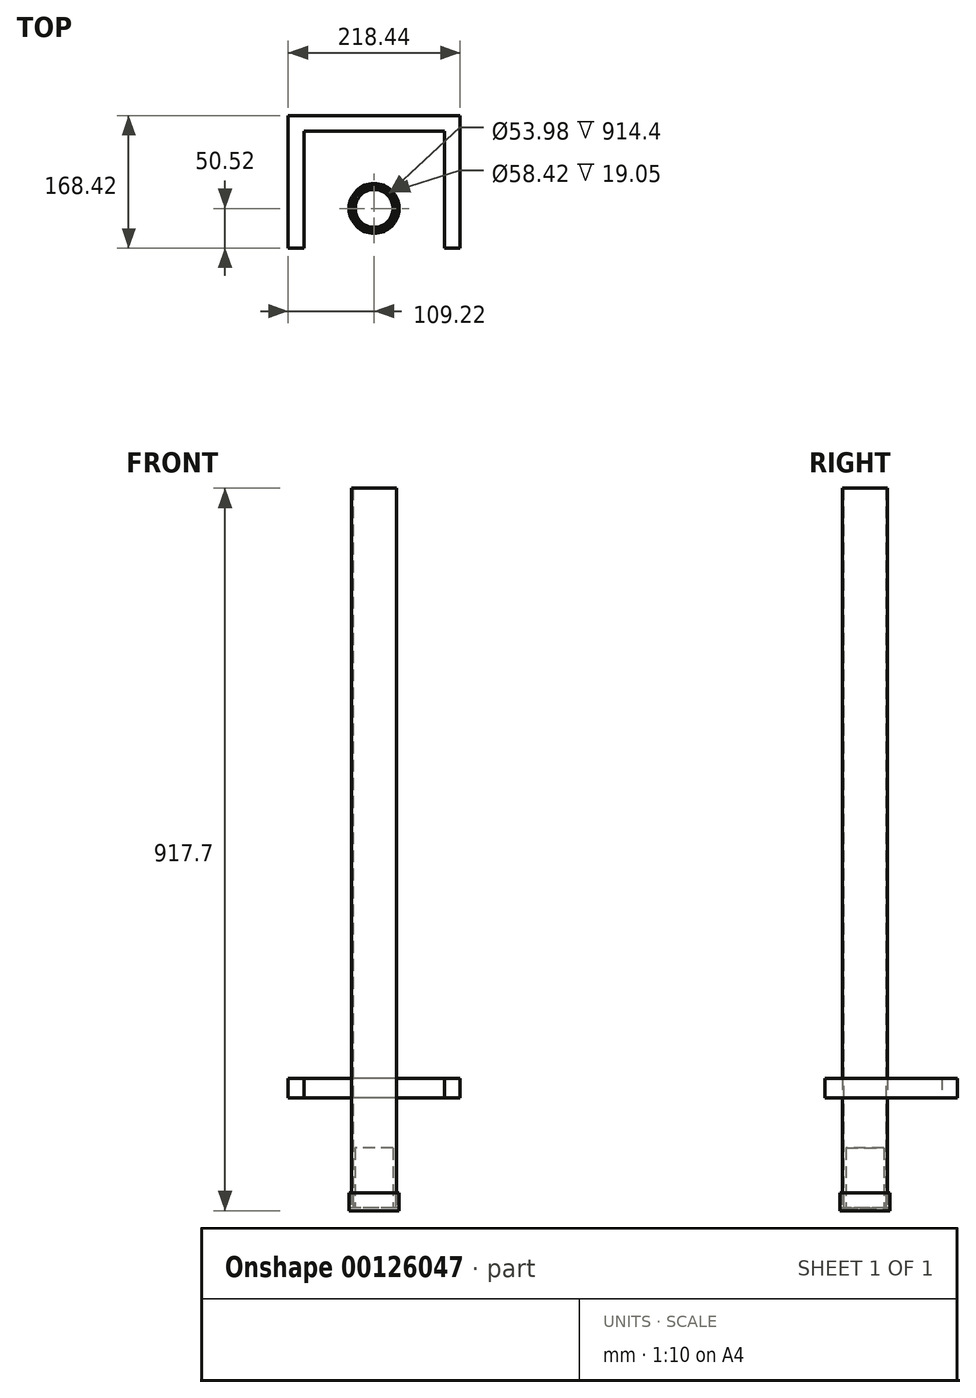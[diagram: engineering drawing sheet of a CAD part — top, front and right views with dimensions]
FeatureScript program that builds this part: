
annotation { "Feature Type Name" : "Feature", "Feature Type Description" : "" }
export const myFeature = defineFeature(function(context is Context, id is Id, definition is map)
    precondition{}
    {
        {
            var Q0;
            Q0=qCreatedBy(makeId("Top.planeOp"),FACE);
            var sketch = newSketch(context, id + "F0", { "sketchPlane" : qUnion([Q0])});
            skCircle(sketch, "E0", {"center": v(0, 0) * mm, "radius": 28.58 * mm});
            skCircle(sketch, "E1", {"center": v(0, 0) * mm, "radius": 26.99 * mm});
            skSolve(sketch);
        }
        {
            var Q0;
            Q0 = qSketchRegion(id + "F0", true);
            extrude(context, id + "F1", {"entities" : qUnion([Q0]), "depth" : 914.4 * mm});
        }
        {
            var Q0;
            Q0=qCreatedBy(makeId("Top.planeOp"),FACE);
            var sketch = newSketch(context, id + "F2", { "sketchPlane" : qUnion([Q0])});
            skCircle(sketch, "E2", {"center": v(0, 0) * mm, "radius": 24 * mm});
            skSolve(sketch);
        }
        {
            var Q0;
            Q0 = qSketchRegion(id + "F2", true);
            var Q1;
            Q1=makeQuery(id+"F2.imprint","IMPRINT",FACE,{"disambiguationData":[TD([[makeQuery(id+"F2.imprint","IMPRINT",EDGE,{"derivedFrom":sQuery(id+"F2.wireOp",EDGE,"E2")}),1.0]])]});
            extrude(context, id + "F3", {"entities" : qUnion([Q0, Q1]), "depth" : 76.2 * mm});
        }
        {
            var Q0;
            Q0=qCreatedBy(makeId("Top.planeOp"),FACE);
            var sketch = newSketch(context, id + "F4", { "sketchPlane" : qUnion([Q0])});
            skCircle(sketch, "E3", {"center": v(0, 0) * mm, "radius": 31.75 * mm});
            skSolve(sketch);
        }
        {
            var Q0;
            Q0=qCreatedBy(makeId("Top.planeOp"),FACE);
            var sketch = newSketch(context, id + "F5", { "sketchPlane" : qUnion([Q0])});
            skCircle(sketch, "E4", {"center": v(0, 0) * mm, "radius": 29.2 * mm});
            skCircle(sketch, "E5", {"center": v(0, 0) * mm, "radius": 31.75 * mm});
            skSolve(sketch);
        }
        {
            var Q0;
            Q0 = qSketchRegion(id + "F5", true);
            extrude(context, id + "F6", {"entities" : qUnion([Q0]), "depth" : 19.05 * mm});
        }
        {
            var Q0;
            Q0 = qSketchRegion(id + "F4", true);
            var Q1;
            Q1=makeQuery(id+"F4.imprint","IMPRINT",FACE,{"disambiguationData":[TD([[makeQuery(id+"F4.imprint","IMPRINT",EDGE,{"derivedFrom":sQuery(id+"F4.wireOp",EDGE,"E3")}),1.0]])]});
            extrude(context, id + "F7", {"entities" : qUnion([Q0, Q1]), "operationType" : NewBodyOperationType.ADD, "oppositeDirection" : true, "depth" : 3.3 * mm});
        }
        {
            var Q0;
            Q0=qCreatedBy(makeId("Top.planeOp"),FACE);
            cPlane(context, id + "F8", {"entities" : qUnion([Q0]), "cplaneType" : CPlaneType.OFFSET, "offset" : 152.4 * mm, "width" : 150 * mm, "height" : 150 * mm});
        }
        {
            var Q0;
            Q0=qCreatedBy(id+"F8.planeOp",FACE);
            var sketch = newSketch(context, id + "F9", { "sketchPlane" : qUnion([Q0])});
            skLineSegment(sketch, "E6.bottom", {"start": v(89.22, 97.9) * mm, "end": v(-89.22, 97.9) * mm});
            skLineSegment(sketch, "E6.left", {"start": v(89.22, 97.9) * mm, "end": v(89.22, -50.52) * mm});
            skLineSegment(sketch, "E6.right", {"start": v(-89.22, 97.9) * mm, "end": v(-89.22, -50.52) * mm});
            skPoint(sketch, "E6.middle", {"position": v(0, 0) * mm});
            skLineSegment(sketch, "E7.bottom", {"start": v(109.22, 117.9) * mm, "end": v(-109.22, 117.9) * mm});
            skLineSegment(sketch, "E7.left", {"start": v(109.22, 117.9) * mm, "end": v(109.22, -50.52) * mm});
            skLineSegment(sketch, "E7.right", {"start": v(-109.22, 117.9) * mm, "end": v(-109.22, -50.52) * mm});
            skLineSegment(sketch, "E8", {"start": v(-89.22, 0) * mm, "end": v(-109.22, 0) * mm, "construction": true});
            skLineSegment(sketch, "E9", {"start": v(89.22, 0) * mm, "end": v(109.22, 0) * mm, "construction": true});
            skLineSegment(sketch, "E10", {"start": v(-109.22, -50.52) * mm, "end": v(-89.22, -50.52) * mm});
            skLineSegment(sketch, "E11.trimOffspring", {"start": v(89.22, -50.52) * mm, "end": v(109.22, -50.52) * mm});
            skSolve(sketch);
        }
        {
            var Q0;
            Q0 = qSketchRegion(id + "F9", true);
            extrude(context, id + "F10", {"entities" : qUnion([Q0]), "endBound" : BoundingType.SYMMETRIC, "depth" : 25 * mm});
        }
    });
